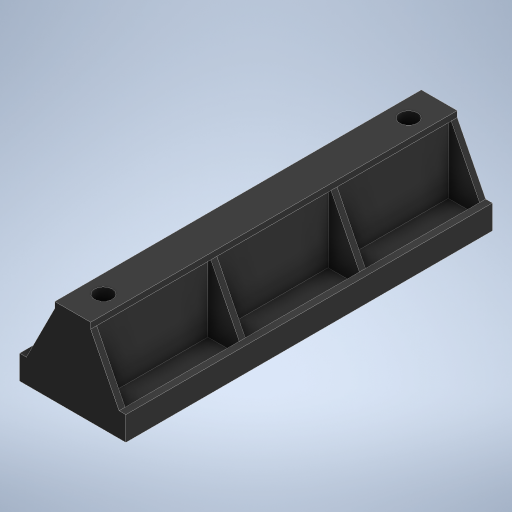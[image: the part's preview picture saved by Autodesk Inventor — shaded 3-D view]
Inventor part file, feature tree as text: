
AUTODESK INVENTOR PART (.ipt)
format: ipt  version: 2024 (Build 280153000, 153)  size: 496,640 bytes
history: native  units: in
note: dims shown in document units (in); Inventor stores cm internally (conversion verified against a paired STEP export)
features: sketch x9, projected_geometry x9, extrude x7, mirror x6, plane x4, loft x1
ambient origin geometry x8: Origin, YZ Plane, XZ Plane, XY Plane, X Axis, Y Axis, Z Axis, Center Point
bodies: Solid1 (feature_tree)
feature tree (36):
  plane  "Work Plane1"
  extrude  "Extrusion2"  Depth=0.4in
  extrude  "Extrusion3"  Depth=0.4in
  mirror  "Mirror1"
  mirror  "Mirror2"
  extrude  "Extrusion4"  Depth=0.0625in
  extrude  "Extrusion5"  Depth=0.0625in
  extrude  "Extrusion6"  Depth=1.184in
  extrude  "Extrusion7"  Depth=1.184in
  extrude  "Extrusion8"  Depth=0.0625in
  plane  "Work Plane2"
  mirror  "Mirror3"
  plane  "Work Plane3"
  loft  "Loft2"
  plane  "Work Plane5"
  mirror  "Mirror7"
  mirror  "Mirror8"
  mirror  "Mirror9"
  sketch  "Sketch2"  dims[d7=0.4in d8=0.4in]
  sketch  "Sketch4"  dims[d9=0.4in d10=0.4in]
  projected_geometry  "Projected Loop1"
  sketch  "Sketch5"  dims[d11=0.125in d12=0.0in d20=0.0625in]
  projected_geometry  "Projected Loop2"
  projected_geometry  "Projected Loop3"
  projected_geometry  "Projected Loop4"
  sketch  "Sketch6"  dims[d21=0.0625in d22=0.592in]
  projected_geometry  "Projected Loop5"
  projected_geometry  "Projected Loop6"
  sketch  "Sketch7"  dims[d23=0.326in d24=1.184in]
  projected_geometry  "Projected Loop7"
  sketch  "Sketch8"  dims[d25=0.0625in d26=1.184in]
  projected_geometry  "Projected Loop8"
  sketch  "Sketch9"  dims[d27=0.326in d28=0.0625in]
  projected_geometry  "Projected Loop9"
  sketch  "Sketch12"  dims[d29=0.0625in d30=0.125in d31=0.0in]
  sketch  "Sketch13"  dims[d32=0.125in d33=0.0in d34=0.125in d35=0.0in d36=0.585in d37=0.0in d38=0.0312in d39=0.0312in d40=0.0625in d41=0.0in d43=0.0312in d44=0.0in d45=-0.155in d50=0.592in d56=0.0in d57=90.0deg d58=0.0in d59=90.0deg d60=0.592in]
